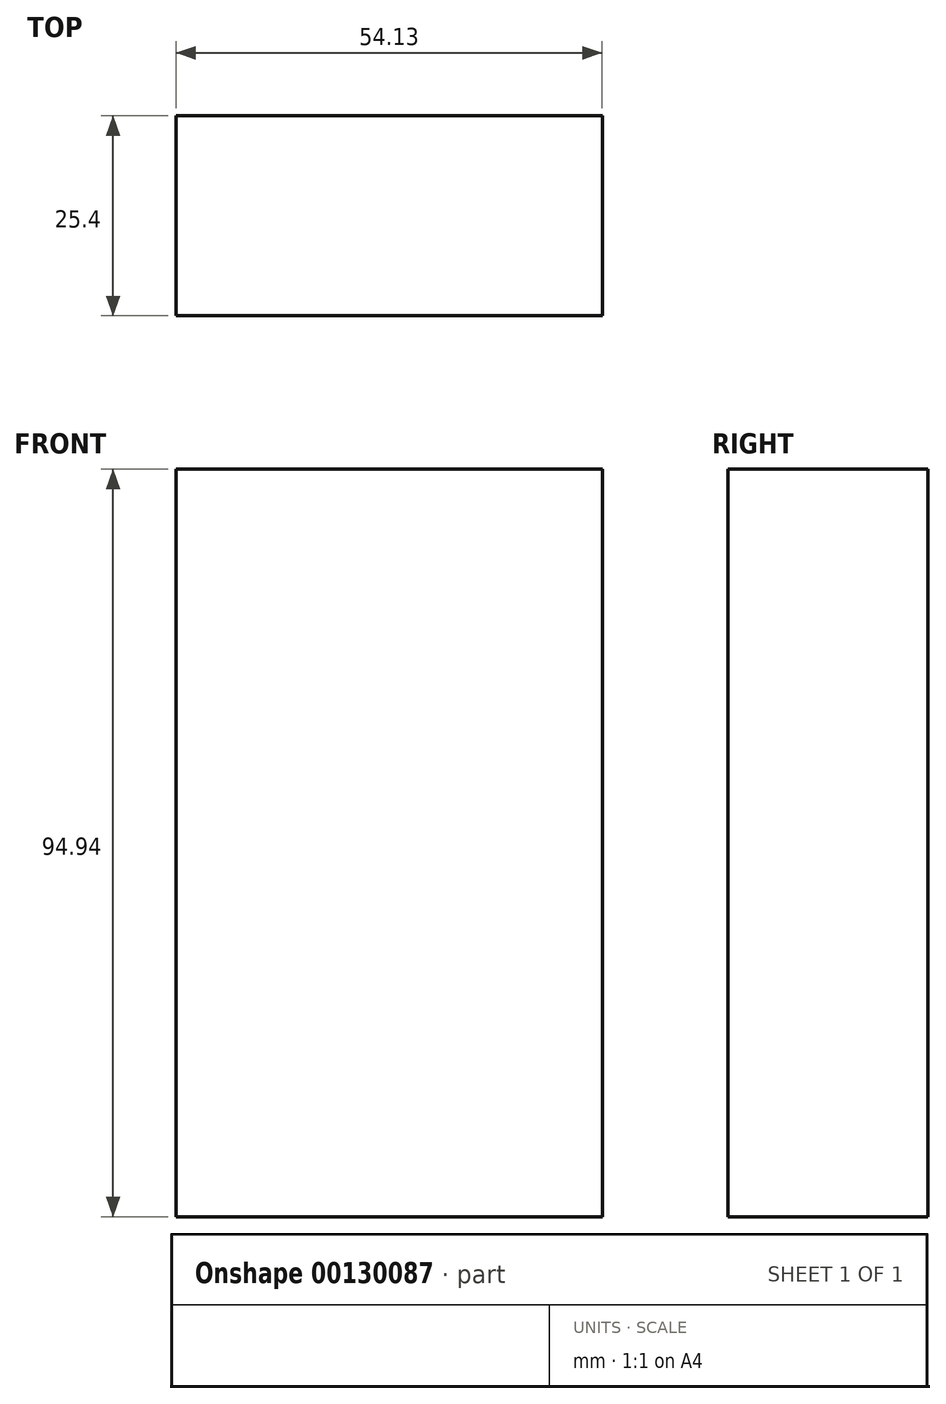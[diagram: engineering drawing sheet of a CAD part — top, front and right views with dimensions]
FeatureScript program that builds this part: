
annotation { "Feature Type Name" : "Feature", "Feature Type Description" : "" }
export const myFeature = defineFeature(function(context is Context, id is Id, definition is map)
    precondition{}
    {
        {
            var Q0;
            Q0=qCreatedBy(makeId("Front.planeOp"),FACE);
            var sketch = newSketch(context, id + "F0", { "sketchPlane" : qUnion([Q0])});
            skLineSegment(sketch, "E0.bottom", {"start": v(0, 35.2) * mm, "end": v(54.13, 35.2) * mm});
            skLineSegment(sketch, "E0.top", {"start": v(0, -59.74) * mm, "end": v(54.13, -59.74) * mm});
            skLineSegment(sketch, "E0.left", {"start": v(0, 35.2) * mm, "end": v(0, -59.74) * mm});
            skLineSegment(sketch, "E0.right", {"start": v(54.13, 35.2) * mm, "end": v(54.13, -59.74) * mm});
            skSolve(sketch);
        }
        {
            var Q0;
            Q0=makeQuery(id+"F0.imprint","IMPRINT",FACE,{"disambiguationData":[TD([[makeQuery(id+"F0.imprint","IMPRINT",EDGE,{"derivedFrom":sQuery(id+"F0.wireOp",EDGE,"E0.bottom")}),-1.0]])]});
            var Q1;
            Q1 = qSketchRegion(id + "F0", true);
            extrude(context, id + "F1", {"entities" : qUnion([Q0, Q1]), "depth" : 25.4 * mm});
        }
    });
